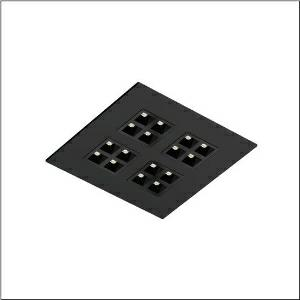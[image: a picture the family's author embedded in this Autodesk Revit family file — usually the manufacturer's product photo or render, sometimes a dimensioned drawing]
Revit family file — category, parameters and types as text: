
# Revit family: silica_r__31_square_51my6lms34ba_bf29
name_source: partatom
category: Lighting Fixtures
units: mm (PartAtom-declared; Revit-internal decimal feet)

## family parameters
Cut with Voids When Loaded = No
Host = Face
Light Source = No
Part Type = Normal
Room Calculation Point = No
Round Connector Dimension = Use Diameter
Shared = No

## types (1)
- --- (1 x LED, 6250 lm, 39 W, 3000K)
    Apparent Load = 39 VA
    CIE Flux Codes = 82 100 100 100 100
    Color Rendering = 80
    Color Temperature = 3000K
    Default Elevation = 1800 mm
    Description = Silica® 31 Square, office luminaire, primary light control with lens, of PMMA, primary anti-glare with reflector, of PC, black, light emission: direct distribution, primary light characteristic: symmetric, installation type: lay-in mounting, LED, rated luminous flux: 4.600lm, luminous efficacy: 166lm/W, light colour: 830, colour temperature: 3000K, control gear: ON/OFF Multilumen, with terminal, 3-pole, mains connection: 220..240V, AC, 50/60Hz, rated input power: 27.7W, luminaire housing, of sheet steel, coated, jet black (RAL 9005), module: M600, length: 595mm, width: 595mm, height: 43mm, protection rating (complete): IP20, insulation class (complete): insulation class II (safety insulation), certification: CE, impact resistance: IK03, permissible operating ambient temperature: -20..+35°C, standard: EN 50419, packaging unit: 1 piece
    Height = 0 mm  [stored 0 ft]
    Lamp = 1 x LED
    Lamp Light Flux = 6250 lm
    Lamp Power = 39 W
    Lamp count = 1
    Length = 595 mm
    Luminous efficacy = 160 lm/W
    Manufacturer = Siteco
    ModVariant = No
    Model = 51MY6LMS34BA
    Mounting Place = Ceiling
    Mounting Type = Recessed
    Number of Poles = 1
    OnlyDefault = Yes
    Power Factor = 1
    Product Name = Silica® 31 Square
    Product group = office luminaire | ceiling recessed
    ProductGroupID = 401
    Protection Class = Protection class II
    Protection Degree = IP 20
    RLX_Detail_Level = 1
    RLX_Emergency_Light_Flux = 0 lm
    RLX_Emergency_Type = 0
    RLX_Emergency_Type_DB = No
    RlxData = <blob elided: 36213 chars, md5=f3872218>
    Socket = socket
    Standby Power = 0 W
    System Light Flux = 6250 lm
    System Power = 39 W
    Type Comments = factory setting: luminous flux: 100 % | (ON | ON | ON | ON) | 1100 mA
    Type Image = l_1313660.jpg
    URL = http://relux.com
    VarID = @adj_036158
    Voltage = 0 V
    Weight = 0.00 kg
    Width = 595 mm

note: [stored X ft] marks values corroborated as IEEE doubles in the binary element streams (Revit-internal decimal feet)

## geometry (parser evidence)
native form markers: Blend x4, Sweep x8
no freeform markers — native parametric forms only
